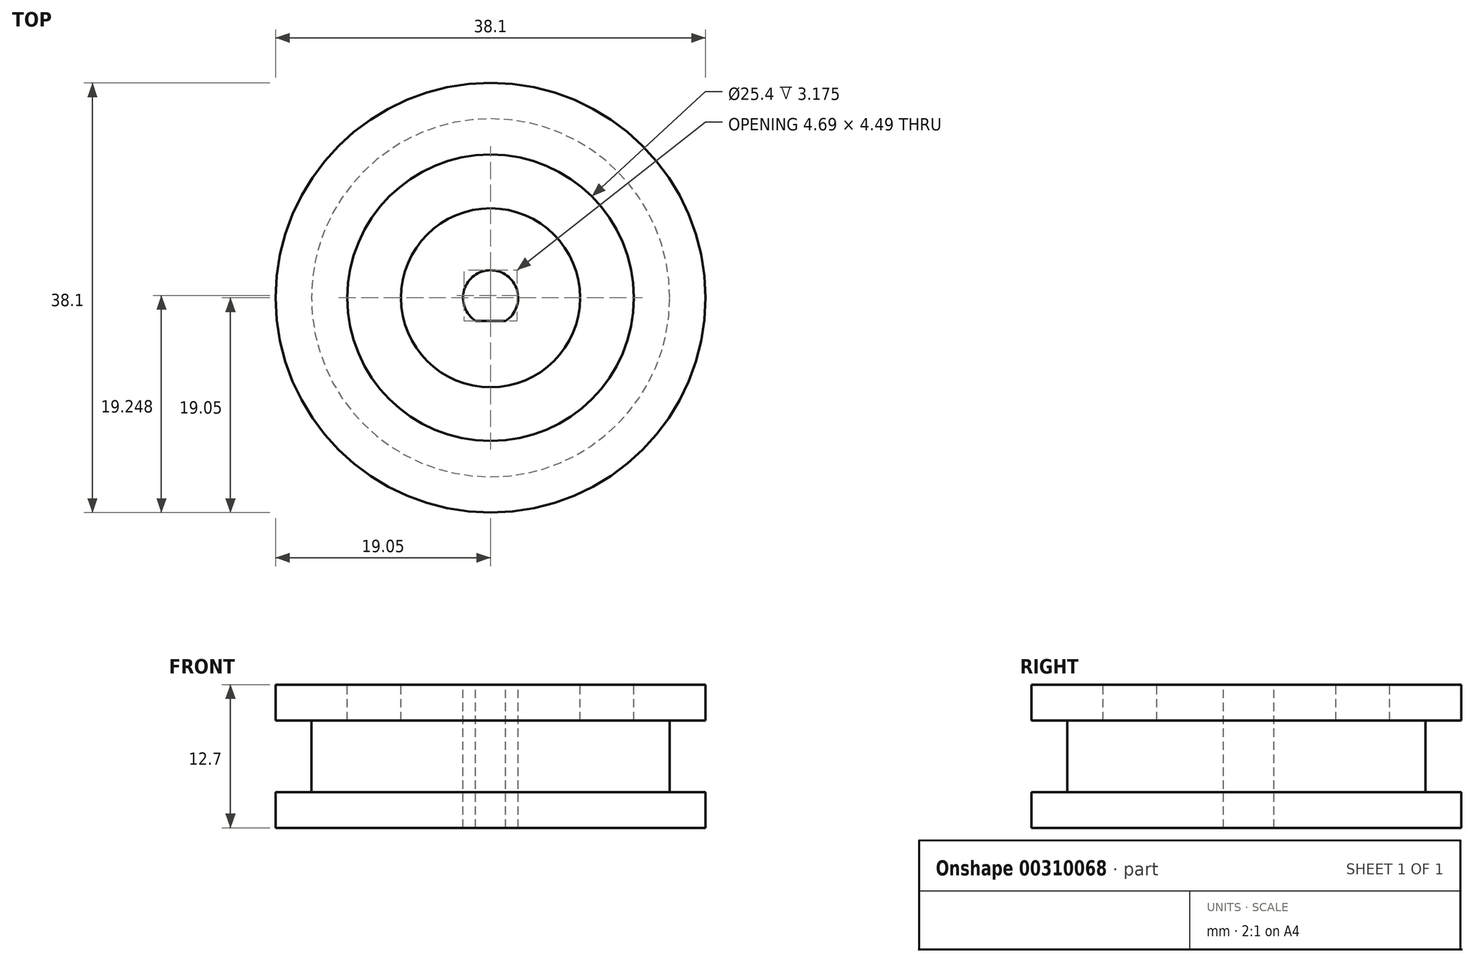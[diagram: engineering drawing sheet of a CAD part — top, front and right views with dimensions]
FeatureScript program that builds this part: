
annotation { "Feature Type Name" : "Feature", "Feature Type Description" : "" }
export const myFeature = defineFeature(function(context is Context, id is Id, definition is map)
    precondition{}
    {
        {
            var Q0;
            Q0=qCreatedBy(makeId("Top.planeOp"),FACE);
            var sketch = newSketch(context, id + "F0", { "sketchPlane" : qUnion([Q0])});
            skCircle(sketch, "E0", {"center": v(0, 0) * mm, "radius": 19.05 * mm});
            skSolve(sketch);
        }
        {
            var Q0;
            Q0 = qSketchRegion(id + "F0", true);
            extrude(context, id + "F1", {"entities" : qUnion([Q0]), "depth" : 3.17 * mm});
        }
        {
            var Q0;
            Q0=makeQuery(id+"F1.opExtrude","CAP_FACE",FACE,{"disambiguationData":[OSD([sQuery(id+"F0.wireOp",EDGE,"E0")])],"isStart":false});
            var sketch = newSketch(context, id + "F2", { "sketchPlane" : qUnion([Q0])});
            skCircle(sketch, "E1", {"center": v(0, 0) * mm, "radius": 15.88 * mm});
            skSolve(sketch);
        }
        {
            var Q0;
            Q0=makeQuery(id+"F2.imprint","IMPRINT",FACE,{"disambiguationData":[TD([[makeQuery(id+"F2.imprint","IMPRINT",EDGE,{"derivedFrom":sQuery(id+"F2.wireOp",EDGE,"E1")}),1.0]])]});
            extrude(context, id + "F3", {"entities" : qUnion([Q0]), "operationType" : NewBodyOperationType.ADD, "depth" : 6.35 * mm});
        }
        {
            var Q0;
            Q0=makeQuery(id+"F3.opExtrude","CAP_FACE",FACE,{"disambiguationData":[OSD([sQuery(id+"F2.wireOp",EDGE,"E1")])],"isStart":false});
            var sketch = newSketch(context, id + "F4", { "sketchPlane" : qUnion([Q0])});
            skCircle(sketch, "E2.0", {"center": v(0, 0) * mm, "radius": 19.05 * mm});
            skSolve(sketch);
        }
        {
            var Q0;
            Q0 = qSketchRegion(id + "F4", true);
            extrude(context, id + "F5", {"entities" : qUnion([Q0]), "operationType" : NewBodyOperationType.ADD, "depth" : 3.17 * mm});
        }
        {
            var Q0;
            Q0=makeQuery(id+"F5.opExtrude","CAP_FACE",FACE,{"disambiguationData":[OSD([sQuery(id+"F4.wireOp",EDGE,"E2.0")])],"isStart":false});
            var sketch = newSketch(context, id + "F6", { "sketchPlane" : qUnion([Q0])});
            skCircle(sketch, "E3", {"center": v(0, 0) * mm, "radius": 12.7 * mm});
            skCircle(sketch, "E4.0", {"center": v(0, 0) * mm, "radius": 7.94 * mm});
            skSolve(sketch);
        }
        {
            var Q0;
            Q0=makeQuery(id+"F6.imprint","IMPRINT",FACE,{"disambiguationData":[TD([[makeQuery(id+"F6.imprint","IMPRINT",EDGE,{"derivedFrom":sQuery(id+"F6.wireOp",EDGE,"E3")}),1.0]])]});
            extrude(context, id + "F7", {"entities" : qUnion([Q0]), "operationType" : NewBodyOperationType.REMOVE, "oppositeDirection" : true, "depth" : 3.17 * mm});
        }
        {
            var Q0;
            {var subQ0=sQuery(id+"F4.wireOp",EDGE,"E2.0");Q0=makeQuery(id+"F7.boolean.opBoolean","SPLIT",FACE,{"disambiguationData":[TD([makeQuery(id+"F5.opExtrude","SWEPT_FACE",FACE,{"disambiguationData":[OSD([subQ0])]})])],"derivedFrom":makeQuery(id+"F5.opExtrude","CAP_FACE",FACE,{"disambiguationData":[OSD([subQ0])],"isStart":false})});}
            var Q1;
            Q1=makeQuery(id+"F1.opExtrude","CAP_FACE",FACE,{"disambiguationData":[OSD([sQuery(id+"F0.wireOp",EDGE,"E0")])],"isStart":true});
            cPlane(context, id + "F8", {"entities" : qUnion([Q0, Q1]), "cplaneType" : CPlaneType.MID_PLANE, "offset" : 25.4 * mm, "width" : 152.4 * mm, "height" : 152.4 * mm});
        }
        {
            var Q0;
            Q0=makeQuery(id+"F7.boolean.opBoolean","SPLIT",FACE,{"disambiguationData":[TD([makeQuery(id+"F7.opExtrude","SWEPT_FACE",FACE,{"disambiguationData":[OSD([sQuery(id+"F6.wireOp",EDGE,"E4.0")])]})])],"derivedFrom":makeQuery(id+"F5.opExtrude","CAP_FACE",FACE,{"disambiguationData":[OSD([sQuery(id+"F4.wireOp",EDGE,"E2.0")])],"isStart":false})});
            var sketch = newSketch(context, id + "F9", { "sketchPlane" : qUnion([Q0])});
            skArc(sketch, "E5", {"start": v(1.34, -2.05) * mm, "mid": v(0, 2.44) * mm, "end": v(-1.34, -2.05) * mm});
            skLineSegment(sketch, "E6", {"start": v(-1.34, -2.05) * mm, "end": v(1.34, -2.05) * mm});
            skLineSegment(sketch, "E7", {"start": v(0, -2.05) * mm, "end": v(0, 2.44) * mm, "construction": true});
            skSolve(sketch);
        }
        {
            var Q0;
            Q0 = qSketchRegion(id + "F9", true);
            extrude(context, id + "F10", {"entities" : qUnion([Q0]), "operationType" : NewBodyOperationType.REMOVE, "endBound" : BoundingType.UP_TO_NEXT, "oppositeDirection" : true, "depth" : 25.4 * mm});
        }
    });
